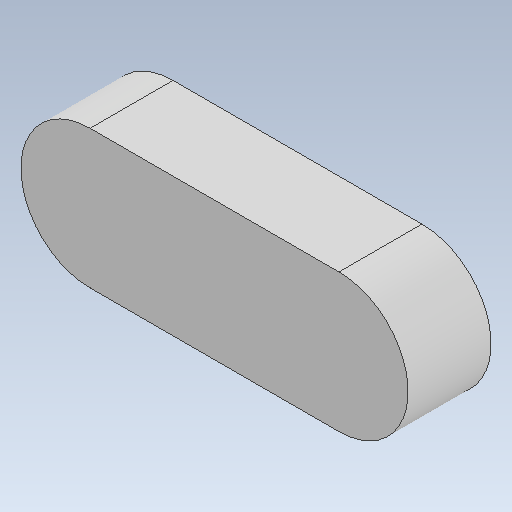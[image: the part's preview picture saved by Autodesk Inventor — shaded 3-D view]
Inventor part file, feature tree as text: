
AUTODESK INVENTOR PART (.ipt)
format: ipt  version: 2020 (Build 240168000, 168)  size: 89,600 bytes
history: native  units: mm
features: other x2, extrude x1, sketch x1, reference x1
ambient origin geometry x8: Origin, YZ Plane, XZ Plane, XY Plane, X Axis, Y Axis, Z Axis, Center Point
bodies: 实体1 (feature_tree)
feature tree (5):
  extrude  "拉伸1"  [1 undecoded]
  sketch  "草图1"  dims[d0=12.0mm d1=0.0mm]
  reference  "参考1"
  other  "<userpath>\Desktop\ME_course_project\课设试试\shaft_try_1.iam"
  other  "shaft_try_1.iam"
note: 1 required parameter value undecoded (feature->parameter linkage not recoverable at this tier; creation-order binding heuristic only, values carry confidence <= 0.55)
